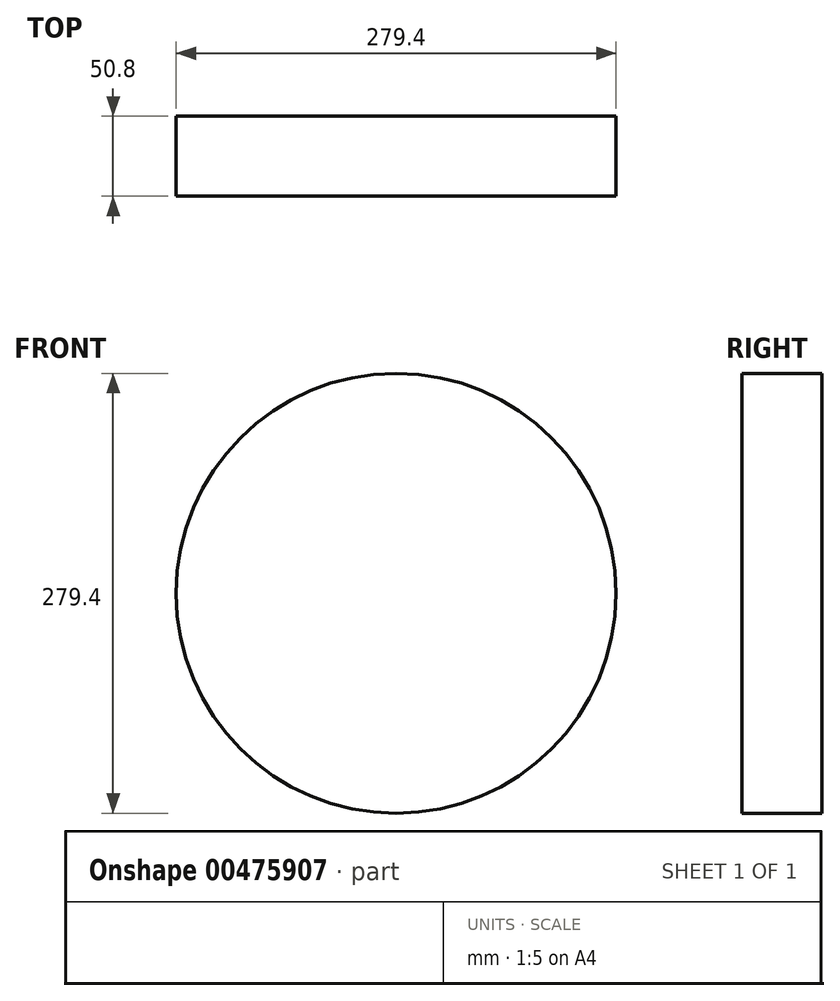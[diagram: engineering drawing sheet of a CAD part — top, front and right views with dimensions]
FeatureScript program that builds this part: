
annotation { "Feature Type Name" : "Feature", "Feature Type Description" : "" }
export const myFeature = defineFeature(function(context is Context, id is Id, definition is map)
    precondition{}
    {
        {
            var Q0;
            Q0=qCreatedBy(makeId("Front.planeOp"),FACE);
            var sketch = newSketch(context, id + "F0", { "sketchPlane" : qUnion([Q0])});
            skCircle(sketch, "E0", {"center": v(0, 0) * mm, "radius": 139.7 * mm});
            skSolve(sketch);
        }
        {
            var Q0;
            Q0=makeQuery(id+"F0.imprint","IMPRINT",FACE,{"disambiguationData":[TD([[makeQuery(id+"F0.imprint","IMPRINT",EDGE,{"derivedFrom":sQuery(id+"F0.wireOp",EDGE,"E0")}),1.0]])]});
            extrude(context, id + "F1", {"entities" : qUnion([Q0]), "endBound" : BoundingType.SYMMETRIC, "depth" : 50.8 * mm, "offsetDistance" : 25.4 * mm});
        }
    });
